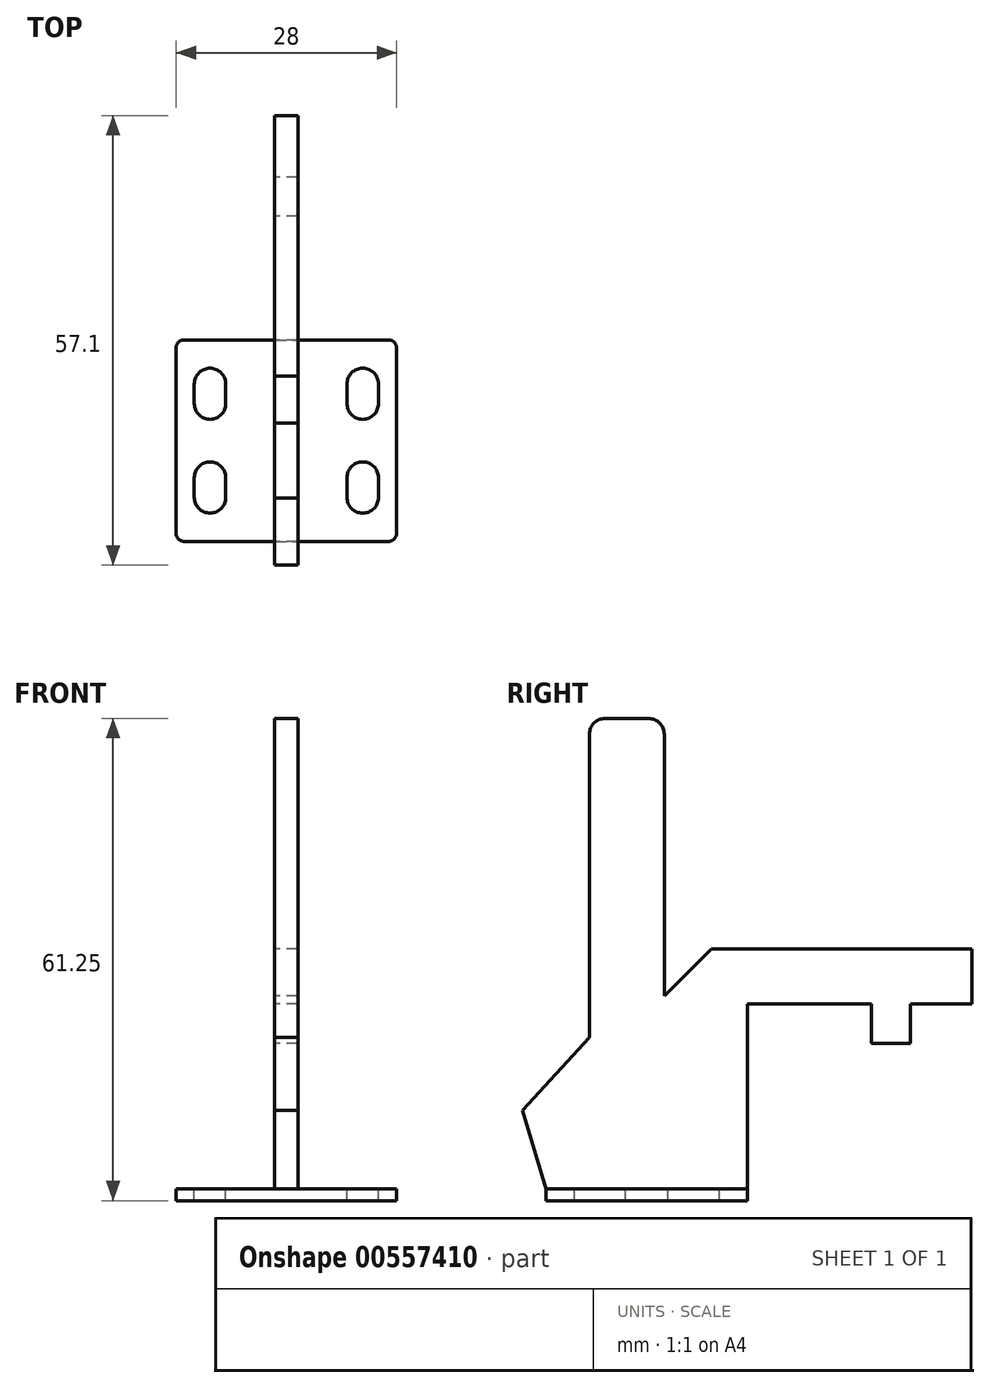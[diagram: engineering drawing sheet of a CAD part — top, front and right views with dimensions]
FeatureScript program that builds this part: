
annotation { "Feature Type Name" : "Feature", "Feature Type Description" : "" }
export const myFeature = defineFeature(function(context is Context, id is Id, definition is map)
    precondition{}
    {
        {
            var Q0;
            Q0=qCreatedBy(makeId("Top.planeOp"),FACE);
            var sketch = newSketch(context, id + "F0", { "sketchPlane" : qUnion([Q0])});
            skLineSegment(sketch, "E0.bottom", {"start": v(1, 0) * mm, "end": v(27, 0) * mm});
            skLineSegment(sketch, "E0.top", {"start": v(1, 25.6) * mm, "end": v(27, 25.6) * mm});
            skLineSegment(sketch, "E0.left", {"start": v(0, 1) * mm, "end": v(0, 24.6) * mm});
            skLineSegment(sketch, "E0.right", {"start": v(28, 1) * mm, "end": v(28, 24.6) * mm});
            skPoint(sketch, "E1.visualSharp", {"position": v(0, 25.6) * mm});
            skArc(sketch, "E1.filletArc", {"start": v(1, 25.6) * mm, "mid": v(0.3, 25.3) * mm, "end": v(0, 24.6) * mm});
            skPoint(sketch, "E2.visualSharp", {"position": v(28, 25.6) * mm});
            skArc(sketch, "E2.filletArc", {"start": v(28, 24.6) * mm, "mid": v(27.7, 25.3) * mm, "end": v(27, 25.6) * mm});
            skPoint(sketch, "E3.visualSharp", {"position": v(28, 0) * mm});
            skArc(sketch, "E3.filletArc", {"start": v(27, 0) * mm, "mid": v(27.7, 0.3) * mm, "end": v(28, 1) * mm});
            skPoint(sketch, "E4.visualSharp", {"position": v(0, 0) * mm});
            skArc(sketch, "E4.filletArc", {"start": v(0, 1) * mm, "mid": v(0.3, 0.3) * mm, "end": v(1, 0) * mm});
            skSolve(sketch);
        }
        {
            var Q0;
            Q0=qSketchRegion(id+"F0",true);
            extrude(context, id + "F1", {"entities" : qUnion([Q0]), "depth" : 1.5 * mm, "offsetDistance" : 25 * mm});
        }
        {
            var Q0;
            Q0=makeQuery(id+"F1.opExtrude","CAP_FACE",FACE,{"disambiguationData":[OSD([sQuery(id+"F0.wireOp",EDGE,"E0.bottom"),sQuery(id+"F0.wireOp",EDGE,"E0.top"),sQuery(id+"F0.wireOp",EDGE,"E0.left"),sQuery(id+"F0.wireOp",EDGE,"E0.right"),sQuery(id+"F0.wireOp",EDGE,"E1.filletArc"),sQuery(id+"F0.wireOp",EDGE,"E2.filletArc"),sQuery(id+"F0.wireOp",EDGE,"E3.filletArc"),sQuery(id+"F0.wireOp",EDGE,"E4.filletArc")])],"isStart":false});
            var sketch = newSketch(context, id + "F2", { "sketchPlane" : qUnion([Q0])});
            skArc(sketch, "E5", {"start": v(6.3, 20) * mm, "mid": v(4.3, 22) * mm, "end": v(2.3, 20) * mm});
            skArc(sketch, "E6", {"start": v(2.3, 17.5) * mm, "mid": v(4.3, 15.5) * mm, "end": v(6.3, 17.5) * mm});
            skLineSegment(sketch, "E7", {"start": v(6.3, 20) * mm, "end": v(6.3, 17.5) * mm});
            skLineSegment(sketch, "E8", {"start": v(2.3, 20) * mm, "end": v(2.3, 17.5) * mm});
            skArc(sketch, "E9", {"start": v(6.3, 8.1) * mm, "mid": v(4.3, 10.1) * mm, "end": v(2.3, 8.1) * mm});
            skArc(sketch, "E10", {"start": v(2.3, 5.6) * mm, "mid": v(4.3, 3.6) * mm, "end": v(6.3, 5.6) * mm});
            skLineSegment(sketch, "E11", {"start": v(6.3, 8.1) * mm, "end": v(6.3, 5.6) * mm});
            skLineSegment(sketch, "E12", {"start": v(2.3, 8.1) * mm, "end": v(2.3, 5.6) * mm});
            skArc(sketch, "E13", {"start": v(25.7, 8.1) * mm, "mid": v(23.7, 10.1) * mm, "end": v(21.7, 8.1) * mm});
            skArc(sketch, "E14", {"start": v(21.7, 5.6) * mm, "mid": v(23.7, 3.6) * mm, "end": v(25.7, 5.6) * mm});
            skLineSegment(sketch, "E15", {"start": v(25.7, 8.1) * mm, "end": v(25.7, 5.6) * mm});
            skLineSegment(sketch, "E16", {"start": v(21.7, 8.1) * mm, "end": v(21.7, 5.6) * mm});
            skArc(sketch, "E17", {"start": v(25.7, 20) * mm, "mid": v(23.7, 22) * mm, "end": v(21.7, 20) * mm});
            skArc(sketch, "E18", {"start": v(21.7, 17.5) * mm, "mid": v(23.7, 15.5) * mm, "end": v(25.7, 17.5) * mm});
            skLineSegment(sketch, "E19", {"start": v(25.7, 20) * mm, "end": v(25.7, 17.5) * mm});
            skLineSegment(sketch, "E20", {"start": v(21.7, 20) * mm, "end": v(21.7, 17.5) * mm});
            skSolve(sketch);
        }
        {
            var Q0;
            Q0=qSketchRegion(id+"F2",true);
            extrude(context, id + "F3", {"entities" : qUnion([Q0]), "operationType" : NewBodyOperationType.REMOVE, "oppositeDirection" : true, "depth" : 25 * mm, "offsetDistance" : 25 * mm});
        }
        {
            var Q0;
            Q0=qCreatedBy(makeId("Right.planeOp"),FACE);
            cPlane(context, id + "F4", {"entities" : qUnion([Q0]), "cplaneType" : CPlaneType.OFFSET, "offset" : 14 * mm, "width" : 150 * mm, "height" : 150 * mm});
        }
        {
            var Q0;
            Q0=qCreatedBy(id+"F4.planeOp",FACE);
            var sketch = newSketch(context, id + "F5", { "sketchPlane" : qUnion([Q0])});
            skLineSegment(sketch, "E21", {"start": v(0, 1.5) * mm, "end": v(-3, 11.5) * mm});
            skLineSegment(sketch, "E22", {"start": v(-3, 11.5) * mm, "end": v(5.5, 20.75) * mm});
            skLineSegment(sketch, "E23", {"start": v(5.5, 20.75) * mm, "end": v(5.5, 59.25) * mm});
            skLineSegment(sketch, "E24", {"start": v(7.5, 61.25) * mm, "end": v(13, 61.25) * mm});
            skLineSegment(sketch, "E25", {"start": v(15, 59.25) * mm, "end": v(15, 26) * mm});
            skLineSegment(sketch, "E26", {"start": v(15, 26) * mm, "end": v(21, 32) * mm});
            skLineSegment(sketch, "E27", {"start": v(21, 32) * mm, "end": v(54.1, 32) * mm});
            skLineSegment(sketch, "E28", {"start": v(54.1, 32) * mm, "end": v(54.1, 25) * mm});
            skLineSegment(sketch, "E29", {"start": v(54.1, 25) * mm, "end": v(25.6, 25) * mm});
            skLineSegment(sketch, "E30", {"start": v(25.6, 25) * mm, "end": v(25.6, 1.5) * mm});
            skLineSegment(sketch, "E31", {"start": v(25.6, 1.5) * mm, "end": v(0, 1.5) * mm});
            skPoint(sketch, "E32.visualSharp", {"position": v(5.5, 61.25) * mm});
            skArc(sketch, "E32.filletArc", {"start": v(7.5, 61.25) * mm, "mid": v(6.09, 60.66) * mm, "end": v(5.5, 59.25) * mm});
            skPoint(sketch, "E33.visualSharp", {"position": v(15, 61.25) * mm});
            skArc(sketch, "E33.filletArc", {"start": v(15, 59.25) * mm, "mid": v(14.41, 60.66) * mm, "end": v(13, 61.25) * mm});
            skSolve(sketch);
        }
        {
            var Q0;
            Q0=makeQuery(id+"F5.imprint","IMPRINT",FACE,{"disambiguationData":[TD([[makeQuery(id+"F5.imprint","IMPRINT",EDGE,{"derivedFrom":sQuery(id+"F5.wireOp",EDGE,"E21")}),-1.0]])]});
            extrude(context, id + "F6", {"entities" : qUnion([Q0]), "operationType" : NewBodyOperationType.ADD, "endBound" : BoundingType.SYMMETRIC, "depth" : 3 * mm, "offsetDistance" : 25 * mm});
        }
        {
            var Q0;
            Q0=makeQuery(id+"F6.opExtrude","SWEPT_FACE",FACE,{"disambiguationData":[OSD([sQuery(id+"F5.wireOp",EDGE,"E29")])]});
            var sketch = newSketch(context, id + "F7", { "sketchPlane" : qUnion([Q0])});
            skLineSegment(sketch, "E34.bottom", {"start": v(15.5, -46.3) * mm, "end": v(12.5, -46.3) * mm});
            skLineSegment(sketch, "E34.top", {"start": v(15.5, -41.3) * mm, "end": v(12.5, -41.3) * mm});
            skLineSegment(sketch, "E34.left", {"start": v(15.5, -46.3) * mm, "end": v(15.5, -41.3) * mm});
            skLineSegment(sketch, "E34.right", {"start": v(12.5, -46.3) * mm, "end": v(12.5, -41.3) * mm});
            skSolve(sketch);
        }
        {
            var Q0;
            Q0=makeQuery(id+"F7.imprint","IMPRINT",FACE,{"disambiguationData":[TD([[makeQuery(id+"F7.imprint","IMPRINT",EDGE,{"derivedFrom":sQuery(id+"F7.wireOp",EDGE,"E34.bottom")}),-1.0]])]});
            extrude(context, id + "F8", {"entities" : qUnion([Q0]), "operationType" : NewBodyOperationType.ADD, "depth" : 5 * mm, "offsetDistance" : 25 * mm});
        }
    });
